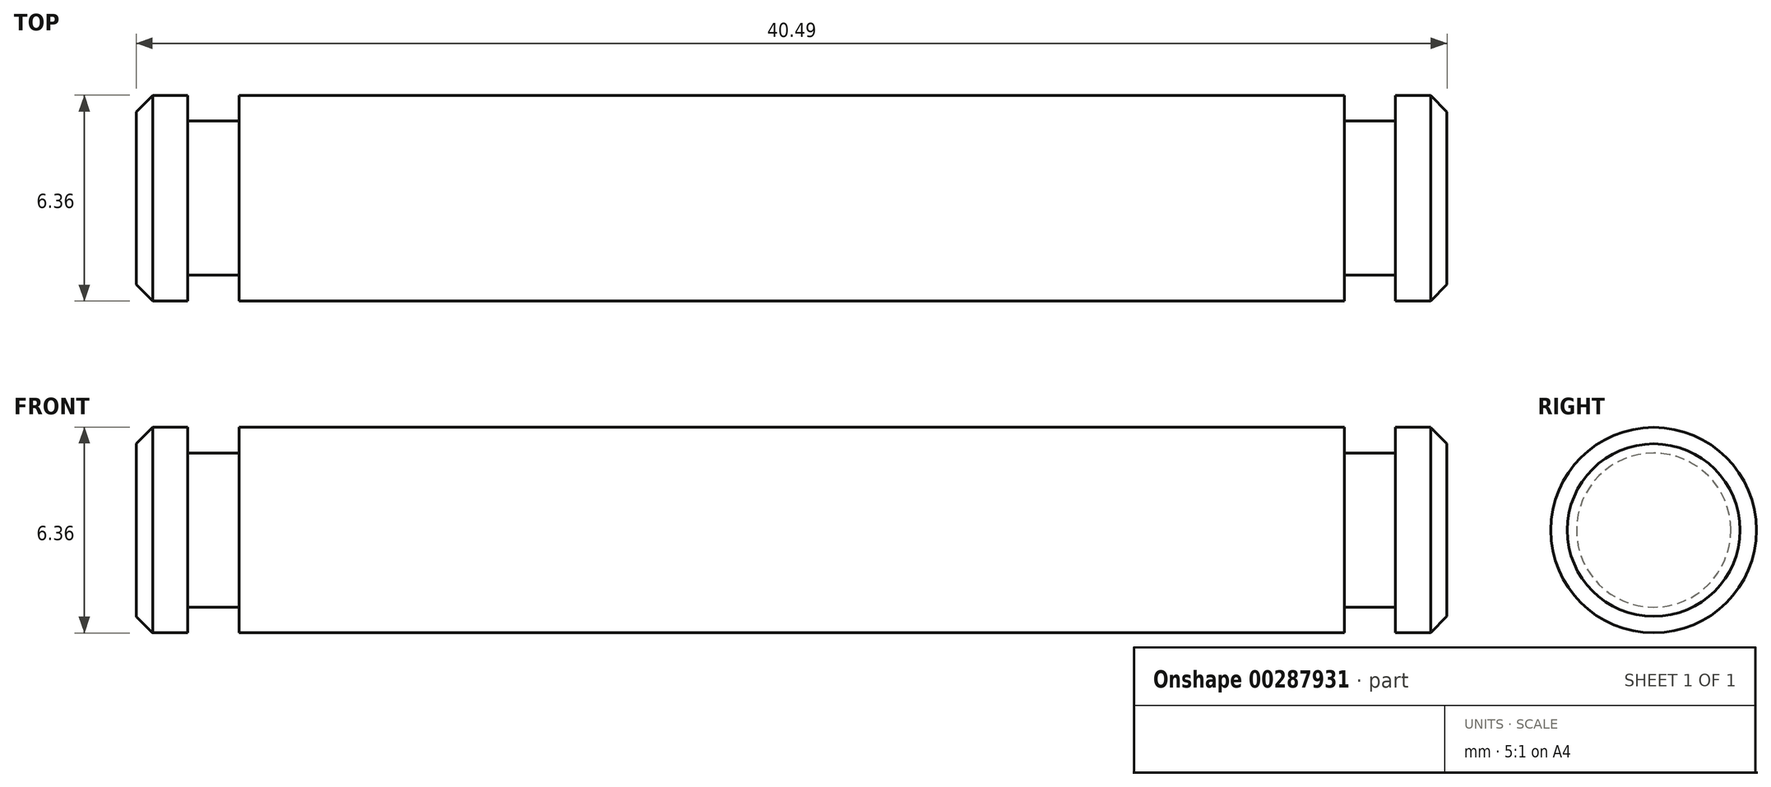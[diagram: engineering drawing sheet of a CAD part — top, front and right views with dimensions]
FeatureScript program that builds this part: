
annotation { "Feature Type Name" : "Feature", "Feature Type Description" : "" }
export const myFeature = defineFeature(function(context is Context, id is Id, definition is map)
    precondition{}
    {
        {
            var Q0;
            Q0=qCreatedBy(makeId("Front.planeOp"),FACE);
            var sketch = newSketch(context, id + "F0", { "sketchPlane" : qUnion([Q0])});
            skLineSegment(sketch, "E0", {"start": v(0, 0) * mm, "end": v(0, 3.18) * mm});
            skLineSegment(sketch, "E1", {"start": v(0, 3.18) * mm, "end": v(1.59, 3.18) * mm});
            skLineSegment(sketch, "E2", {"start": v(1.59, 3.18) * mm, "end": v(1.59, 2.38) * mm});
            skLineSegment(sketch, "E3", {"start": v(1.59, 2.38) * mm, "end": v(3.17, 2.38) * mm});
            skLineSegment(sketch, "E4", {"start": v(3.17, 2.38) * mm, "end": v(3.17, 3.18) * mm});
            skLineSegment(sketch, "E5", {"start": v(3.18, 3.18) * mm, "end": v(37.31, 3.18) * mm});
            skLineSegment(sketch, "E6", {"start": v(37.31, 3.18) * mm, "end": v(37.31, 2.38) * mm});
            skLineSegment(sketch, "E7", {"start": v(37.31, 2.38) * mm, "end": v(38.9, 2.38) * mm});
            skLineSegment(sketch, "E8", {"start": v(38.9, 2.38) * mm, "end": v(38.9, 3.18) * mm});
            skLineSegment(sketch, "E9", {"start": v(38.9, 3.18) * mm, "end": v(40.49, 3.18) * mm});
            skLineSegment(sketch, "E10", {"start": v(40.49, 3.18) * mm, "end": v(40.49, 0) * mm});
            skLineSegment(sketch, "E11", {"start": v(40.49, 0) * mm, "end": v(0, 0) * mm});
            skSolve(sketch);
        }
        {
            var Q0;
            Q0=makeQuery(id+"F0.imprint","IMPRINT",FACE,{"disambiguationData":[TD([[makeQuery(id+"F0.imprint","IMPRINT",EDGE,{"derivedFrom":sQuery(id+"F0.wireOp",EDGE,"E0")}),-1.0]])]});
            var Q1;
            Q1=sQuery(id+"F0.wireOp",EDGE,"E11");
            revolve(context, id + "F1", {"entities" : qUnion([Q0]), "axis" : qUnion([Q1]), "revolveType" : RevolveType.FULL});
        }
        {
            var Q0;
            Q0=makeQuery(id+"F1.opRevolve","SWEPT_EDGE",EDGE,{"disambiguationData":[OSD([sQuery(id+"F0.wireOp",EDGE,"E9"),sQuery(id+"F0.wireOp",EDGE,"E10")])]});
            var Q1;
            Q1=makeQuery(id+"F1.opRevolve","SWEPT_EDGE",EDGE,{"disambiguationData":[OSD([sQuery(id+"F0.wireOp",EDGE,"E0"),sQuery(id+"F0.wireOp",EDGE,"E1")])]});
            chamfer(context, id + "F2", {"entities" : qUnion([Q0, Q1]), "width" : 0.5 * mm, "tangentPropagation" : true});
        }
    });
